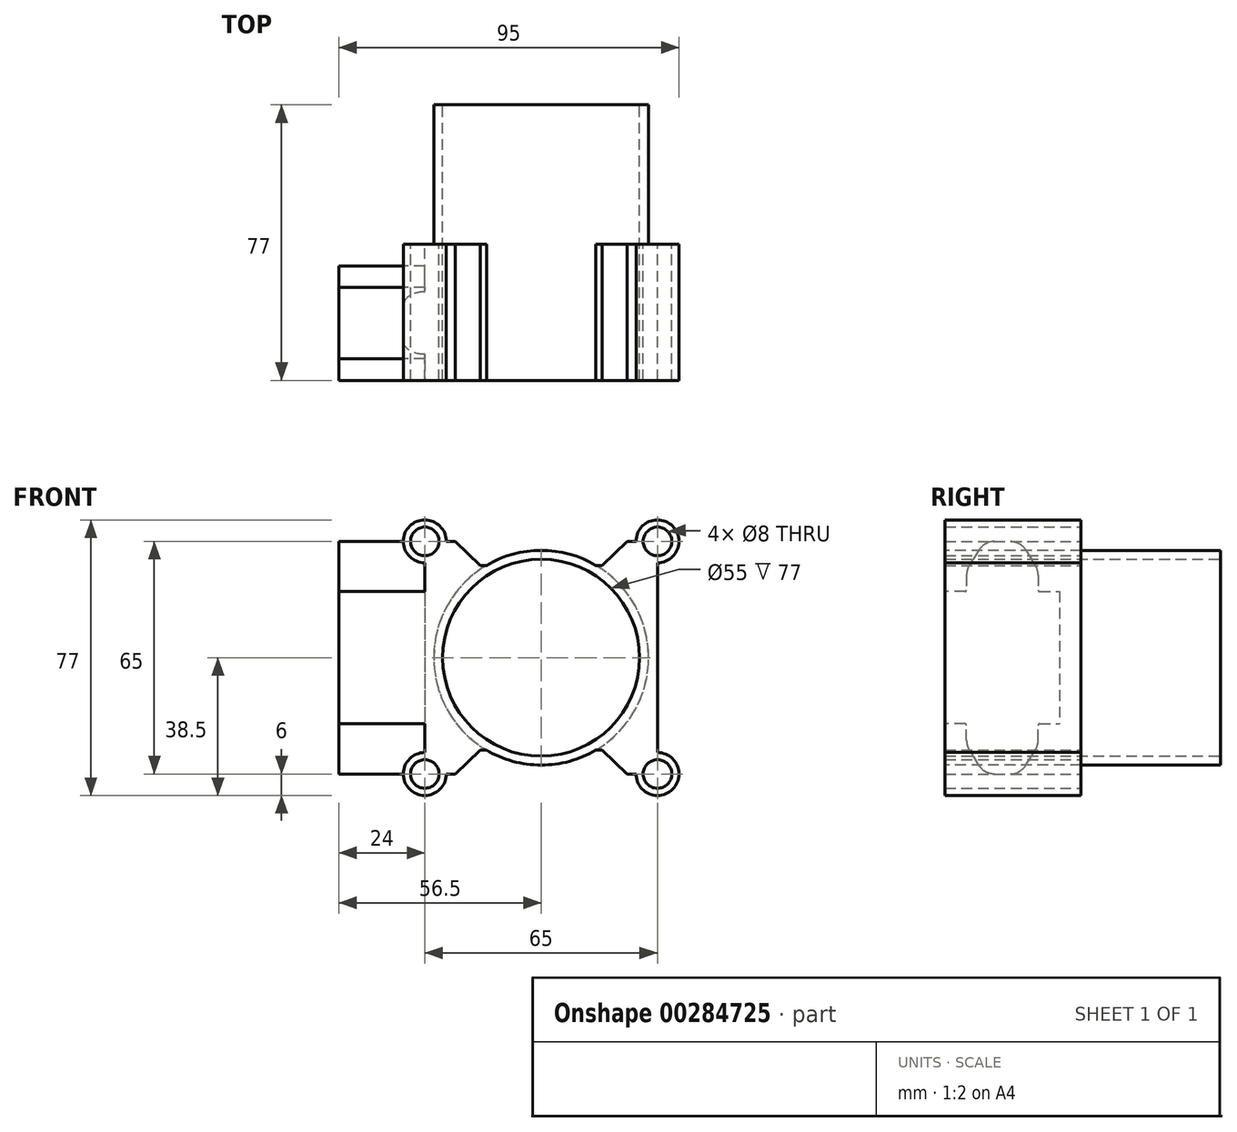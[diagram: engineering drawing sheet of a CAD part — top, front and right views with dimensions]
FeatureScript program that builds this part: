
annotation { "Feature Type Name" : "Feature", "Feature Type Description" : "" }
export const myFeature = defineFeature(function(context is Context, id is Id, definition is map)
    precondition{}
    {
        {
            var Q0;
            Q0=qCreatedBy(makeId("Front.planeOp"),FACE);
            var sketch = newSketch(context, id + "F0", { "sketchPlane" : qUnion([Q0])});
            skLineSegment(sketch, "E0.bottom", {"start": v(32.5, 32.5) * mm, "end": v(-32.5, 32.5) * mm});
            skLineSegment(sketch, "E0.top", {"start": v(32.5, -32.5) * mm, "end": v(-32.5, -32.5) * mm});
            skLineSegment(sketch, "E0.left", {"start": v(32.5, 32.5) * mm, "end": v(32.5, -32.5) * mm});
            skLineSegment(sketch, "E0.right", {"start": v(-32.5, 32.5) * mm, "end": v(-32.5, -32.5) * mm});
            skPoint(sketch, "E0.middle", {"position": v(0, 0) * mm});
            skCircle(sketch, "E1", {"center": v(0, 0) * mm, "radius": 30 * mm});
            skCircle(sketch, "E2", {"center": v(0, 0) * mm, "radius": 27.5 * mm});
            skCircle(sketch, "E3", {"center": v(-32.5, 32.5) * mm, "radius": 6 * mm});
            skCircle(sketch, "E4", {"center": v(32.5, 32.5) * mm, "radius": 6 * mm});
            skCircle(sketch, "E5", {"center": v(-32.5, -32.5) * mm, "radius": 6 * mm});
            skCircle(sketch, "E6", {"center": v(32.5, -32.5) * mm, "radius": 6 * mm});
            skCircle(sketch, "E7", {"center": v(-32.5, 32.5) * mm, "radius": 4 * mm});
            skCircle(sketch, "E8", {"center": v(32.5, 32.5) * mm, "radius": 4 * mm});
            skCircle(sketch, "E9", {"center": v(32.5, -32.5) * mm, "radius": 4 * mm});
            skCircle(sketch, "E10", {"center": v(-32.5, -32.5) * mm, "radius": 4 * mm});
            skSolve(sketch);
        }
        {
            var Q0;
            Q0=qSketchRegion(id+"F0",true);
            var Q1;
            Q1=makeQuery(id+"F0.imprint","IMPRINT",FACE,{"disambiguationData":[TD([[makeQuery(id+"F0.imprint","IMPRINT",EDGE,{"derivedFrom":sQuery(id+"F0.wireOp",EDGE,"E1")}),1.0]])]});
            extrude(context, id + "F1", {"entities" : qUnion([Q0, Q1]), "depth" : 38 * mm});
        }
        {
            var Q0;
            Q0=qCreatedBy(makeId("Front.planeOp"),FACE);
            cPlane(context, id + "F2", {"entities" : qUnion([Q0]), "cplaneType" : CPlaneType.OFFSET, "offset" : 1 * mm, "width" : 150 * mm, "height" : 150 * mm});
        }
        {
            var Q0;
            Q0=qCreatedBy(id+"F2.planeOp",FACE);
            var sketch = newSketch(context, id + "F3", { "sketchPlane" : qUnion([Q0])});
            skCircle(sketch, "E11.0", {"center": v(0, 0) * mm, "radius": 30 * mm});
            skCircle(sketch, "E12", {"center": v(0, 0) * mm, "radius": 27.5 * mm});
            skSolve(sketch);
        }
        {
            var Q0;
            Q0=qSketchRegion(id+"F3",true);
            extrude(context, id + "F4", {"entities" : qUnion([Q0]), "operationType" : NewBodyOperationType.ADD, "oppositeDirection" : true, "depth" : 40 * mm});
        }
        {
            var Q0;
            Q0=qCreatedBy(makeId("Top.planeOp"),FACE);
            cPlane(context, id + "F5", {"entities" : qUnion([Q0]), "cplaneType" : CPlaneType.OFFSET, "offset" : 32.5 * mm, "oppositeDirection" : true, "width" : 150 * mm, "height" : 150 * mm});
        }
        {
            var Q0;
            Q0=qCreatedBy(id+"F5.planeOp",FACE);
            var sketch = newSketch(context, id + "F6", { "sketchPlane" : qUnion([Q0])});
            skLineSegment(sketch, "E13.0", {"start": v(-32.5, -38) * mm, "end": v(-32.5, 0) * mm});
            skPoint(sketch, "E14", {"position": v(-32.5, -6) * mm});
            skLineSegment(sketch, "E15", {"start": v(-32.5, -6) * mm, "end": v(-56.5, -6) * mm});
            skLineSegment(sketch, "E16", {"start": v(-56.5, -6) * mm, "end": v(-56.5, -38) * mm});
            skLineSegment(sketch, "E17", {"start": v(-56.5, -38) * mm, "end": v(-32.5, -38) * mm});
            skSolve(sketch);
        }
        {
            var Q0;
            Q0=qSketchRegion(id+"F6",true);
            extrude(context, id + "F7", {"entities" : qUnion([Q0]), "operationType" : NewBodyOperationType.ADD, "depth" : 65 * mm});
        }
        {
            var Q0;
            Q0=makeQuery(id+"F7.opExtrude","SWEPT_FACE",FACE,{"disambiguationData":[OSD([sQuery(id+"F6.wireOp",EDGE,"E16")])]});
            var sketch = newSketch(context, id + "F8", { "sketchPlane" : qUnion([Q0])});
            skLineSegment(sketch, "E18.0", {"start": v(6, 32.5) * mm, "end": v(6, -32.5) * mm});
            skLineSegment(sketch, "E19.0", {"start": v(6, 32.5) * mm, "end": v(38, 32.5) * mm});
            skLineSegment(sketch, "E20.0", {"start": v(38, 32.5) * mm, "end": v(38, -32.5) * mm});
            skLineSegment(sketch, "E21.0", {"start": v(6, -32.5) * mm, "end": v(38, -32.5) * mm});
            skPoint(sketch, "E22", {"position": v(22, 32.5) * mm});
            skPoint(sketch, "E23", {"position": v(27, 32.5) * mm});
            skPoint(sketch, "E24", {"position": v(17, 32.5) * mm});
            skPoint(sketch, "E25", {"position": v(22, 18.5) * mm});
            skLineSegment(sketch, "E26", {"start": v(22, 32.5) * mm, "end": v(22, -32.5) * mm, "construction": true});
            skLineSegment(sketch, "E27", {"start": v(6, 0) * mm, "end": v(38, 0) * mm, "construction": true});
            skPoint(sketch, "E28", {"position": v(12, 24.5) * mm});
            skPoint(sketch, "E29", {"position": v(12, 18.5) * mm});
            skLineSegment(sketch, "E30", {"start": v(22, 32.5) * mm, "end": v(19.77, 32.5) * mm});
            skLineSegment(sketch, "E31", {"start": v(15.53, 30.15) * mm, "end": v(12.76, 25.72) * mm});
            skLineSegment(sketch, "E32", {"start": v(12, 23.07) * mm, "end": v(12, 18.9) * mm});
            skLineSegment(sketch, "E33", {"start": v(12, 18.5) * mm, "end": v(22, 18.5) * mm});
            skLineSegment(sketch, "E34.MirrorCS", {"start": v(22, 32.5) * mm, "end": v(24.23, 32.5) * mm});
            skLineSegment(sketch, "E35.MirrorCS", {"start": v(28.47, 30.15) * mm, "end": v(31.24, 25.72) * mm});
            skLineSegment(sketch, "E36.MirrorCS", {"start": v(32, 23.07) * mm, "end": v(32, 18.9) * mm});
            skLineSegment(sketch, "E37.MirrorCS", {"start": v(32, 18.5) * mm, "end": v(22, 18.5) * mm});
            skLineSegment(sketch, "E38", {"start": v(11.6, 18.5) * mm, "end": v(6, 18.5) * mm});
            skLineSegment(sketch, "E39", {"start": v(32.4, 18.5) * mm, "end": v(38, 18.5) * mm});
            skLineSegment(sketch, "E40.MirrorCS", {"start": v(15.53, -30.15) * mm, "end": v(12.76, -25.72) * mm});
            skLineSegment(sketch, "E41.MirrorCS", {"start": v(12, -23.07) * mm, "end": v(12, -18.9) * mm});
            skLineSegment(sketch, "E42.MirrorCS", {"start": v(11.6, -18.5) * mm, "end": v(6, -18.5) * mm});
            skLineSegment(sketch, "E43.MirrorCS", {"start": v(22, -32.5) * mm, "end": v(19.77, -32.5) * mm});
            skLineSegment(sketch, "E44.MirrorCS", {"start": v(22, -32.5) * mm, "end": v(24.23, -32.5) * mm});
            skLineSegment(sketch, "E45.MirrorCS", {"start": v(28.47, -30.15) * mm, "end": v(31.24, -25.72) * mm});
            skLineSegment(sketch, "E46.MirrorCS", {"start": v(32, -23.07) * mm, "end": v(32, -18.9) * mm});
            skLineSegment(sketch, "E47.MirrorCS", {"start": v(32.4, -18.5) * mm, "end": v(38, -18.5) * mm});
            skArc(sketch, "E48.filletArc", {"start": v(19.77, 32.5) * mm, "mid": v(17.35, 31.87) * mm, "end": v(15.53, 30.15) * mm});
            skArc(sketch, "E49.filletArc", {"start": v(28.47, 30.15) * mm, "mid": v(26.65, 31.87) * mm, "end": v(24.23, 32.5) * mm});
            skArc(sketch, "E50.filletArc", {"start": v(12.76, 25.72) * mm, "mid": v(12.2, 24.44) * mm, "end": v(12, 23.07) * mm});
            skPoint(sketch, "E51.visualSharp", {"position": v(32, 24.5) * mm});
            skArc(sketch, "E51.filletArc", {"start": v(32, 23.07) * mm, "mid": v(31.8, 24.44) * mm, "end": v(31.24, 25.72) * mm});
            skArc(sketch, "E52.filletArc", {"start": v(11.6, 18.5) * mm, "mid": v(11.88, 18.62) * mm, "end": v(12, 18.9) * mm});
            skPoint(sketch, "E53.visualSharp", {"position": v(32, 18.5) * mm});
            skArc(sketch, "E53.filletArc", {"start": v(32, 18.9) * mm, "mid": v(32.12, 18.62) * mm, "end": v(32.4, 18.5) * mm});
            skPoint(sketch, "E54.visualSharp", {"position": v(17, -32.5) * mm});
            skArc(sketch, "E54.filletArc", {"start": v(15.53, -30.15) * mm, "mid": v(17.35, -31.87) * mm, "end": v(19.77, -32.5) * mm});
            skPoint(sketch, "E55.visualSharp", {"position": v(27, -32.5) * mm});
            skArc(sketch, "E55.filletArc", {"start": v(24.23, -32.5) * mm, "mid": v(26.65, -31.87) * mm, "end": v(28.47, -30.15) * mm});
            skPoint(sketch, "E56.visualSharp", {"position": v(32, -24.5) * mm});
            skArc(sketch, "E56.filletArc", {"start": v(31.24, -25.72) * mm, "mid": v(31.8, -24.44) * mm, "end": v(32, -23.07) * mm});
            skPoint(sketch, "E57.visualSharp", {"position": v(12, -24.5) * mm});
            skArc(sketch, "E57.filletArc", {"start": v(12, -23.07) * mm, "mid": v(12.2, -24.44) * mm, "end": v(12.76, -25.72) * mm});
            skPoint(sketch, "E58.visualSharp", {"position": v(12, -18.5) * mm});
            skArc(sketch, "E58.filletArc", {"start": v(12, -18.9) * mm, "mid": v(11.88, -18.62) * mm, "end": v(11.6, -18.5) * mm});
            skPoint(sketch, "E59.visualSharp", {"position": v(32, -18.5) * mm});
            skArc(sketch, "E59.filletArc", {"start": v(32.4, -18.5) * mm, "mid": v(32.12, -18.62) * mm, "end": v(32, -18.9) * mm});
            skSolve(sketch);
        }
        {
            var Q0;
            {var subQ0=sQuery(id+"F8.wireOp",EDGE,"E40.MirrorCS");Q0=makeQuery(id+"F8.imprint","IMPRINT",FACE,{"disambiguationData":[TD([[makeQuery(id+"F8.imprint","IMPRINT",EDGE,{"derivedFrom":subQ0}),1.0]])]});}
            var Q1;
            {var subQ3=sQuery(id+"F8.wireOp",EDGE,"E45.MirrorCS");Q1=makeQuery(id+"F8.imprint","IMPRINT",FACE,{"disambiguationData":[TD([[makeQuery(id+"F8.imprint","IMPRINT",EDGE,{"derivedFrom":subQ3}),-1.0]])]});}
            var Q2;
            {var subQ0=sQuery(id+"F8.wireOp",EDGE,"E31");Q2=makeQuery(id+"F8.imprint","IMPRINT",FACE,{"disambiguationData":[TD([[makeQuery(id+"F8.imprint","IMPRINT",EDGE,{"derivedFrom":subQ0}),-1.0]])]});}
            var Q3;
            {var subQ1=sQuery(id+"F8.wireOp",EDGE,"E35.MirrorCS");Q3=makeQuery(id+"F8.imprint","IMPRINT",FACE,{"disambiguationData":[TD([[makeQuery(id+"F8.imprint","IMPRINT",EDGE,{"derivedFrom":subQ1}),1.0]])]});}
            extrude(context, id + "F9", {"entities" : qUnion([Q0, Q1, Q2, Q3]), "operationType" : NewBodyOperationType.REMOVE, "oppositeDirection" : true, "depth" : 24 * mm});
        }
        {
            var Q0;
            {var subQ0=sQuery(id+"F0.wireOp",EDGE,"E4");var subQ1=sQuery(id+"F0.wireOp",EDGE,"E0.bottom");var subQ2=makeQuery(id+"F0.imprint","INTERSECT",VERTEX,{"derivedFrom":[subQ1,subQ0]});Q0=makeQuery(id+"F0.imprint","IMPRINT",FACE,{"disambiguationData":[TD([[makeQuery(id+"F0.imprint","IMPRINT",EDGE,{"disambiguationData":[TD([[subQ2,1.0]])],"derivedFrom":subQ1}),-1.0]])]});}
            var Q1;
            {var subQ0=sQuery(id+"F0.wireOp",EDGE,"E3");var subQ1=sQuery(id+"F0.wireOp",EDGE,"E0.bottom");var subQ2=makeQuery(id+"F0.imprint","INTERSECT",VERTEX,{"derivedFrom":[subQ1,subQ0]});Q1=makeQuery(id+"F0.imprint","IMPRINT",FACE,{"disambiguationData":[TD([[makeQuery(id+"F0.imprint","IMPRINT",EDGE,{"disambiguationData":[TD([[subQ2,-1.0]])],"derivedFrom":subQ1}),-1.0]])]});}
            var Q2;
            {var subQ0=sQuery(id+"F0.wireOp",EDGE,"E6");var subQ1=sQuery(id+"F0.wireOp",EDGE,"E0.top");var subQ2=makeQuery(id+"F0.imprint","INTERSECT",VERTEX,{"derivedFrom":[subQ1,subQ0]});Q2=makeQuery(id+"F0.imprint","IMPRINT",FACE,{"disambiguationData":[TD([[makeQuery(id+"F0.imprint","IMPRINT",EDGE,{"disambiguationData":[TD([[subQ2,1.0]])],"derivedFrom":subQ1}),1.0]])]});}
            var Q3;
            {var subQ0=sQuery(id+"F0.wireOp",EDGE,"E5");var subQ1=sQuery(id+"F0.wireOp",EDGE,"E0.top");var subQ2=makeQuery(id+"F0.imprint","INTERSECT",VERTEX,{"derivedFrom":[subQ1,subQ0]});Q3=makeQuery(id+"F0.imprint","IMPRINT",FACE,{"disambiguationData":[TD([[makeQuery(id+"F0.imprint","IMPRINT",EDGE,{"disambiguationData":[TD([[subQ2,-1.0]])],"derivedFrom":subQ1}),1.0]])]});}
            extrude(context, id + "F10", {"entities" : qUnion([Q0, Q1, Q2, Q3]), "operationType" : NewBodyOperationType.ADD, "depth" : 38 * mm});
        }
        {
            var Q0;
            Q0=makeQuery(id+"F1.opExtrude","CAP_FACE",FACE,{"disambiguationData":[OSD([sQuery(id+"F0.wireOp",EDGE,"E0.bottom"),sQuery(id+"F0.wireOp",EDGE,"E0.top"),sQuery(id+"F0.wireOp",EDGE,"E0.left"),sQuery(id+"F0.wireOp",EDGE,"E0.right"),sQuery(id+"F0.wireOp",EDGE,"E1"),sQuery(id+"F0.wireOp",EDGE,"E3"),sQuery(id+"F0.wireOp",EDGE,"E4"),sQuery(id+"F0.wireOp",EDGE,"E5"),sQuery(id+"F0.wireOp",EDGE,"E6"),sQuery(id+"F0.wireOp",EDGE,"E7"),sQuery(id+"F0.wireOp",EDGE,"E8"),sQuery(id+"F0.wireOp",EDGE,"E9"),sQuery(id+"F0.wireOp",EDGE,"E10")])],"isStart":true});
            var sketch = newSketch(context, id + "F11", { "sketchPlane" : qUnion([Q0])});
            skArc(sketch, "E60.0", {"start": v(-32.5, 26.5) * mm, "mid": v(-36.74, 36.74) * mm, "end": v(-26.5, 32.5) * mm});
            skPoint(sketch, "E61", {"position": v(-32.5, 38.5) * mm});
            skPoint(sketch, "E62", {"position": v(0, 32.5) * mm});
            skPoint(sketch, "E63", {"position": v(17, 32.5) * mm});
            skPoint(sketch, "E64", {"position": v(-17, 32.5) * mm});
            skCircle(sketch, "E65.0", {"center": v(0, 0) * mm, "radius": 30 * mm});
            skPoint(sketch, "E66", {"position": v(-27.5, 35.81) * mm});
            skArc(sketch, "E67.0", {"start": v(26.5, 32.5) * mm, "mid": v(36.74, 36.74) * mm, "end": v(32.5, 26.5) * mm});
            skPoint(sketch, "E68", {"position": v(27.3, 35.5) * mm});
            skPoint(sketch, "E69", {"position": v(-17, 25.81) * mm});
            skLineSegment(sketch, "E70", {"start": v(-27.5, 35.81) * mm, "end": v(-17, 25.81) * mm});
            skLineSegment(sketch, "E71", {"start": v(0, 32.5) * mm, "end": v(0, -32.5) * mm, "construction": true});
            skLineSegment(sketch, "E72", {"start": v(-32.5, 0) * mm, "end": v(32.5, 0) * mm, "construction": true});
            skLineSegment(sketch, "E73.MirrorCS", {"start": v(0, -32.5) * mm, "end": v(0, 32.5) * mm, "construction": true});
            skLineSegment(sketch, "E74.MirrorCS", {"start": v(-27.5, -35.81) * mm, "end": v(-17, -25.81) * mm});
            skArc(sketch, "E75.MirrorCS", {"start": v(-32.5, -26.5) * mm, "mid": v(-36.74, -36.74) * mm, "end": v(-26.5, -32.5) * mm});
            skLineSegment(sketch, "E76.0", {"start": v(-24.02, 32.5) * mm, "end": v(24.02, 32.5) * mm});
            skLineSegment(sketch, "E77.MirrorCS", {"start": v(-24.02, -32.5) * mm, "end": v(24.02, -32.5) * mm});
            skLineSegment(sketch, "E78.MirrorCS", {"start": v(27.5, 35.81) * mm, "end": v(17, 25.81) * mm});
            skLineSegment(sketch, "E79.MirrorCS", {"start": v(27.5, -35.81) * mm, "end": v(17, -25.81) * mm});
            skArc(sketch, "E80.MirrorCS", {"start": v(32.5, 26.5) * mm, "mid": v(36.74, 36.74) * mm, "end": v(26.5, 32.5) * mm});
            skArc(sketch, "E81.MirrorCS", {"start": v(32.5, -26.5) * mm, "mid": v(36.74, -36.74) * mm, "end": v(26.5, -32.5) * mm});
            skPoint(sketch, "E82.orphan", {"position": v(-26.5, -32.5) * mm});
            skPoint(sketch, "E83.orphan", {"position": v(26.5, -32.5) * mm});
            skLineSegment(sketch, "E84", {"start": v(-17, 25.81) * mm, "end": v(-15.29, 25.81) * mm});
            skLineSegment(sketch, "E85.MirrorCS", {"start": v(17, 25.81) * mm, "end": v(15.29, 25.81) * mm});
            skLineSegment(sketch, "E86.MirrorCS", {"start": v(17, -25.81) * mm, "end": v(15.29, -25.81) * mm});
            skLineSegment(sketch, "E87.MirrorCS", {"start": v(-17, -25.81) * mm, "end": v(-15.29, -25.81) * mm});
            skSolve(sketch);
        }
        {
            var Q0;
            {var subQ1=sQuery(id+"F11.wireOp",EDGE,"E76.0");Q0=makeQuery(id+"F11.imprint","IMPRINT",FACE,{"disambiguationData":[TD([[makeQuery(id+"F11.imprint","IMPRINT",EDGE,{"derivedFrom":subQ1}),-1.0]])]});}
            var Q1;
            {var subQ1=sQuery(id+"F11.wireOp",EDGE,"E77.MirrorCS");Q1=makeQuery(id+"F11.imprint","IMPRINT",FACE,{"disambiguationData":[TD([[makeQuery(id+"F11.imprint","IMPRINT",EDGE,{"derivedFrom":subQ1}),1.0]])]});}
            extrude(context, id + "F12", {"entities" : qUnion([Q0, Q1]), "operationType" : NewBodyOperationType.REMOVE, "oppositeDirection" : true, "depth" : 38 * mm});
        }
        {
            var Q0;
            {var subQ0=sQuery(id+"F0.wireOp",EDGE,"E10");var subQ1=sQuery(id+"F0.wireOp",EDGE,"E5");var subQ2=sQuery(id+"F0.wireOp",EDGE,"E0.right");var subQ3=sQuery(id+"F0.wireOp",EDGE,"E0.top");var subQ4=sQuery(id+"F0.wireOp",EDGE,"E7");var subQ5=sQuery(id+"F0.wireOp",EDGE,"E3");var subQ6=sQuery(id+"F0.wireOp",EDGE,"E0.bottom");Q0=makeQuery(id+"F10.boolean.opBoolean","MERGE",FACE,{"derivedFrom":[makeQuery(id+"F7.boolean.opBoolean","MERGE",FACE,{"derivedFrom":[makeQuery(id+"F1.opExtrude","CAP_FACE",FACE,{"disambiguationData":[OSD([subQ6,subQ3,sQuery(id+"F0.wireOp",EDGE,"E0.left"),subQ2,sQuery(id+"F0.wireOp",EDGE,"E2"),subQ5,sQuery(id+"F0.wireOp",EDGE,"E4"),subQ1,sQuery(id+"F0.wireOp",EDGE,"E6"),subQ4,sQuery(id+"F0.wireOp",EDGE,"E8"),sQuery(id+"F0.wireOp",EDGE,"E9"),subQ0])],"isStart":false}),makeQuery(id+"F7.opExtrude","SWEPT_FACE",FACE,{"disambiguationData":[OSD([sQuery(id+"F6.wireOp",EDGE,"E17")])]})]}),makeQuery(id+"F10.opExtrude","CAP_FACE",FACE,{"disambiguationData":[OSD([subQ6,subQ2,subQ5,subQ4])],"isStart":false}),makeQuery(id+"F10.opExtrude","CAP_FACE",FACE,{"disambiguationData":[OSD([subQ3,subQ2,subQ1,subQ0])],"isStart":false})]});}
            var sketch = newSketch(context, id + "F13", { "sketchPlane" : qUnion([Q0])});
            skCircle(sketch, "E88.0", {"center": v(-32.5, 32.5) * mm, "radius": 4 * mm});
            skCircle(sketch, "E89.0", {"center": v(-32.5, -32.5) * mm, "radius": 4 * mm});
            skSolve(sketch);
        }
        {
            var Q0;
            Q0=qSketchRegion(id+"F13",true);
            extrude(context, id + "F14", {"entities" : qUnion([Q0]), "operationType" : NewBodyOperationType.REMOVE, "oppositeDirection" : true, "depth" : 38 * mm});
        }
    });
